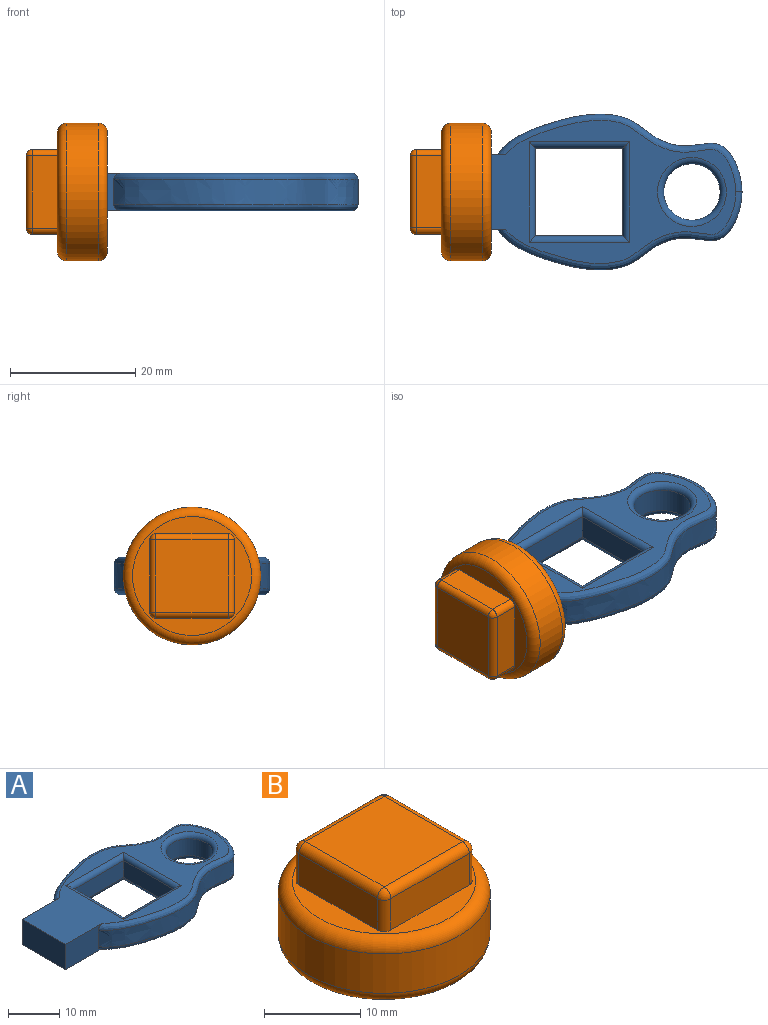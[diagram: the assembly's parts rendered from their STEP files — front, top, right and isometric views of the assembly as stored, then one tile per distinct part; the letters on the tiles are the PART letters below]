
ASSEMBLY  parts=2 mates=1
PART A: 26 faces, bbox 48.3x25.2x6.3 mm
  f0: plane 12x6mm, normal (-1,0,0), area 72mm2, adj f1,f9,f10,f11
  f1: plane 10.59x6.35mm, normal (0,-1,0), area 54.5mm2, adj f0,f2,f10,f11,f12,f19
  f2: extruded ~39x12.43mm, area 188.6mm2, adj f1,f3,f12,f19
  f3: extruded ~39x12.43mm, area 188.6mm2, adj f2,f9,f13,f20
  f4: plane 14x4mm, normal (0,-1,0), area 56mm2, adj f5,f8,f16,f23
  f5: plane 14x4mm, normal (-1,0,0), area 56mm2, adj f4,f6,f15,f22
  f6: plane 14x4mm, normal (0,1,0), area 56mm2, adj f5,f8,f17,f24
  f7: cylinder r=4.5mm len=9mm, axis (0,0,-1), area 113.1mm2, adj f14,f21
  f8: plane 14x4mm, normal (1,0,0), area 56mm2, adj f4,f6,f18,f25
  f9: plane 10.59x6.35mm, normal (0,1,0), area 54.5mm2, adj f0,f3,f10,f11,f13,f20
  f10: plane 47x22.86mm, normal (0,0,1), area 404.2mm2, adj f0,f1,f9,f19,f20,f21,f22,f23
  f11: plane 47x22.86mm, normal (0,0,-1), area 404.2mm2, adj f0,f1,f9,f12,f13,f14,f15,f16
  f12: bspline ~39.1x12.63mm, area 72.1mm2, adj f1,f2,f11,f13
  f13: bspline ~39.1x12.69mm, area 72mm2, adj f3,f9,f11,f12
  f14: torus R=5.5mm, axis (0,0,1), area 48mm2, adj f7,f11
  f15: cylinder r=1mm len=16mm, axis (0,-1,0), area 23.6mm2, adj f5,f11,f16,f17
  f16: cylinder r=1mm len=16mm, axis (1,0,0), area 23.6mm2, adj f4,f11,f15,f18
  f17: cylinder r=1mm len=16mm, axis (-1,0,0), area 23.6mm2, adj f6,f11,f15,f18
  f18: cylinder r=1mm len=16mm, axis (0,1,0), area 23.6mm2, adj f8,f11,f16,f17
  f19: bspline ~39.1x12.69mm, area 72mm2, adj f1,f2,f10,f20
  f20: bspline ~39.1x12.63mm, area 72.1mm2, adj f3,f9,f10,f19
  f21: torus R=5.5mm, axis (0,0,1), area 48mm2, adj f7,f10
  f22: cylinder r=1mm len=16mm, axis (0,1,0), area 23.6mm2, adj f5,f10,f23,f24
  f23: cylinder r=1mm len=16mm, axis (-1,0,0), area 23.6mm2, adj f4,f10,f22,f25
  f24: cylinder r=1mm len=16mm, axis (1,0,0), area 23.6mm2, adj f6,f10,f22,f25
  f25: cylinder r=1mm len=16mm, axis (0,-1,0), area 23.6mm2, adj f8,f10,f23,f24
PART B: 27 faces, bbox 23.8x23.8x13 mm
  f0: plane 19x19mm, normal (0,0,1), area 102.1mm2, adj f7,f10,f11,f12,f13,f15,f17,f20
  f1: plane 19x19mm, normal (0,0,-1), area 202.3mm2, adj f3,f4,f5,f6,f8
  f2: cylinder r=11mm len=22mm, axis (0,0,1), area 345.6mm2, adj f7,f8
  f3: plane 8x6.5mm, normal (-1,0,0), area 52mm2, adj f1,f4,f6,f9
  f4: plane 12.5x8mm, normal (0,1,0), area 100mm2, adj f1,f3,f5,f9
  f5: plane 8x6.5mm, normal (1,0,0), area 52mm2, adj f1,f4,f6,f9
  f6: plane 12.5x8mm, normal (0,-1,0), area 100mm2, adj f1,f3,f5,f9
  f7: torus R=9.5mm, axis (0,0,1), area 154.8mm2, adj f0,f2
  f8: torus R=9.5mm, axis (0,0,1), area 154.8mm2, adj f1,f2
  f9: plane 12.5x6.5mm, normal (0,0,-1), area 81.2mm2, adj f3,f4,f5,f6
  f10: plane 11.5x4mm, normal (1,0,0), area 46mm2, adj f0,f17,f23,f26
  f11: plane 11.5x4mm, normal (0,1,0), area 46mm2, adj f0,f20,f24,f26
  f12: plane 11.5x4mm, normal (-1,0,0), area 46mm2, adj f0,f15,f19,f20
  f13: plane 11.5x4mm, normal (0,-1,0), area 46mm2, adj f0,f15,f17,f18
  f14: plane 11.5x11.5mm, normal (0,0,1), area 132.2mm2, adj f18,f19,f23,f24
  f15: cylinder r=1mm len=4mm, axis (0,0,1), area 6.3mm2, adj f0,f12,f13,f16
  f16: sphere r=1mm, area 1.6mm2, adj f15,f18,f19
  f17: cylinder r=1mm len=4mm, axis (0,0,-1), area 6.3mm2, adj f0,f10,f13,f21
  f18: cylinder r=1mm len=11.5mm, axis (-1,0,0), area 18.1mm2, adj f13,f14,f16,f21
  f19: cylinder r=1mm len=11.5mm, axis (0,1,0), area 18.1mm2, adj f12,f14,f16,f22
  f20: cylinder r=1mm len=4mm, axis (0,0,-1), area 6.3mm2, adj f0,f11,f12,f22
  f21: sphere r=1mm, area 1.6mm2, adj f17,f18,f23
  f22: sphere r=1mm, area 1.6mm2, adj f19,f20,f24
  f23: cylinder r=1mm len=11.5mm, axis (0,-1,0), area 18.1mm2, adj f10,f14,f21,f25
  f24: cylinder r=1mm len=11.5mm, axis (1,0,0), area 18.1mm2, adj f11,f14,f22,f25
  f25: sphere r=1mm, area 1.6mm2, adj f23,f24,f26
  f26: cylinder r=1mm len=4mm, axis (0,0,1), area 6.3mm2, adj f0,f10,f11,f25
PLACE A t=(-12.06,4.47,-8.05)mm fixed
PLACE B rot(axis=(0.58,-0.58,-0.58),120deg) t=(-12.06,4.47,-5.05)mm
MATE fastened A.f0 <-> B.f2  axis (-1,0,0) through (-12.06,4.47,-5.05)mm
